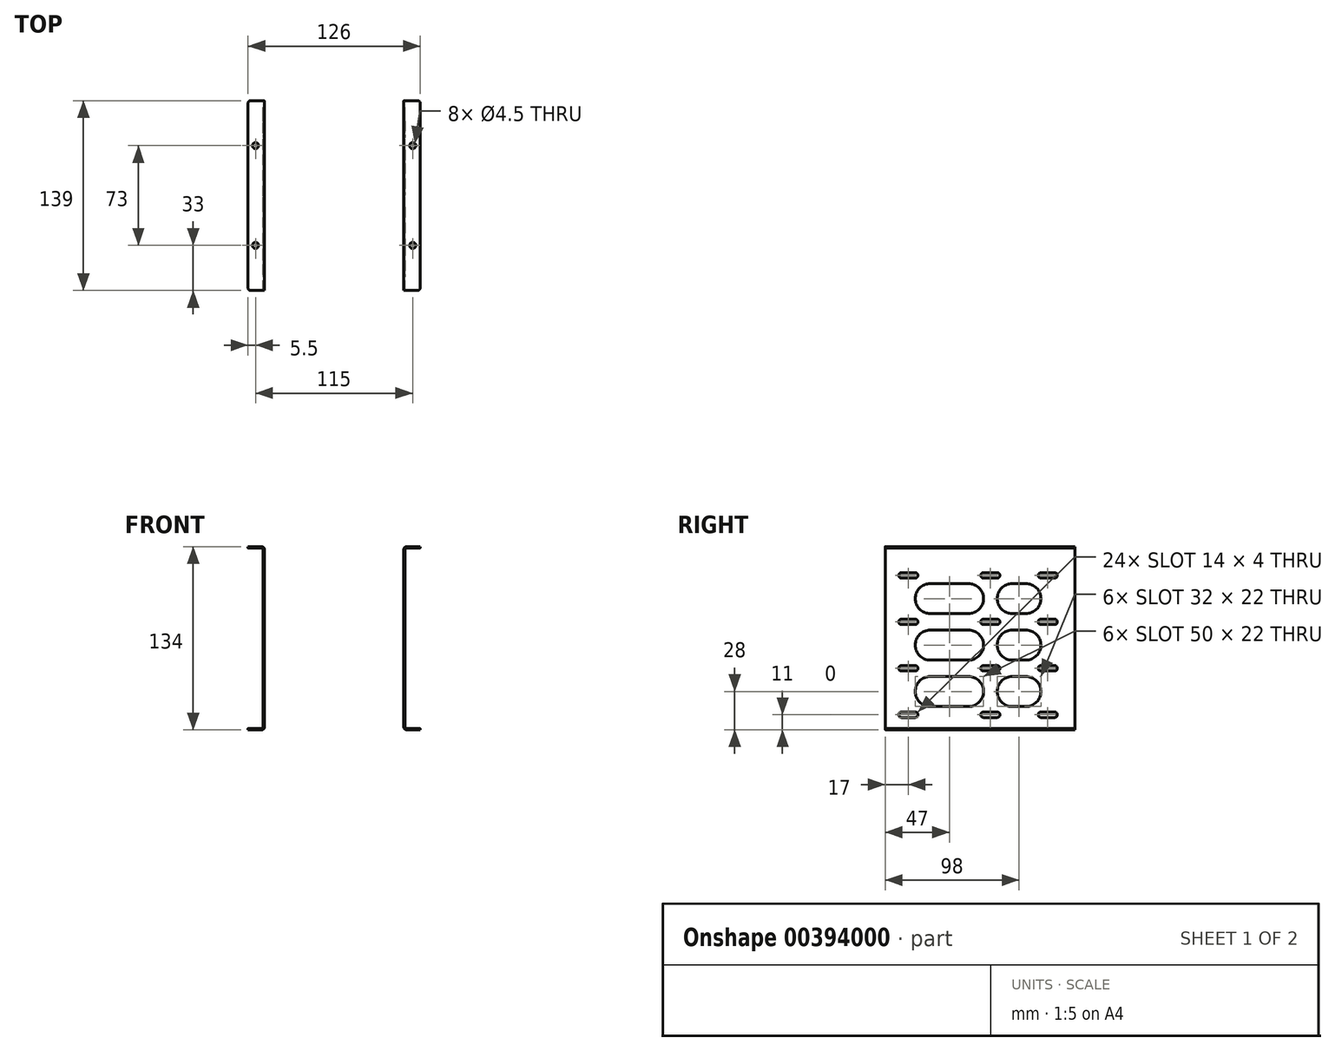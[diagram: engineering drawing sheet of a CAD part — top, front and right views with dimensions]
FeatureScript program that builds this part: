
annotation { "Feature Type Name" : "Feature", "Feature Type Description" : "" }
export const myFeature = defineFeature(function(context is Context, id is Id, definition is map)
    precondition{}
    {
        {
            var Q0;
            Q0=qCreatedBy(makeId("Front.planeOp"),FACE);
            var sketch = newSketch(context, id + "F0", { "sketchPlane" : qUnion([Q0])});
            skLineSegment(sketch, "E0", {"start": v(0, 0) * mm, "end": v(10, 0) * mm});
            skLineSegment(sketch, "E1", {"start": v(12, 2) * mm, "end": v(12, 132) * mm});
            skLineSegment(sketch, "E2", {"start": v(10, 134) * mm, "end": v(0, 134) * mm});
            skLineSegment(sketch, "E3.0", {"start": v(0, 1) * mm, "end": v(10, 1) * mm});
            skLineSegment(sketch, "E4.0", {"start": v(11, 2) * mm, "end": v(11, 132) * mm});
            skLineSegment(sketch, "E5.0", {"start": v(10, 133) * mm, "end": v(0, 133) * mm});
            skLineSegment(sketch, "E6", {"start": v(0, 133) * mm, "end": v(0, 134) * mm});
            skLineSegment(sketch, "E7", {"start": v(0, 0) * mm, "end": v(0, 1) * mm});
            skPoint(sketch, "E8.visualSharp", {"position": v(11, 1) * mm});
            skArc(sketch, "E8.filletArc", {"start": v(10, 1) * mm, "mid": v(10.7, 1.3) * mm, "end": v(11, 2) * mm});
            skPoint(sketch, "E9.visualSharp", {"position": v(12, 0) * mm});
            skArc(sketch, "E9.filletArc", {"start": v(10, 0) * mm, "mid": v(11.41, 0.59) * mm, "end": v(12, 2) * mm});
            skPoint(sketch, "E10.visualSharp", {"position": v(11, 133) * mm});
            skArc(sketch, "E10.filletArc", {"start": v(11, 132) * mm, "mid": v(10.7, 132.7) * mm, "end": v(10, 133) * mm});
            skPoint(sketch, "E11.visualSharp", {"position": v(12, 134) * mm});
            skArc(sketch, "E11.filletArc", {"start": v(12, 132) * mm, "mid": v(11.41, 133.41) * mm, "end": v(10, 134) * mm});
            skSolve(sketch);
        }
        {
            var Q0;
            Q0=qSketchRegion(id+"F0",true);
            extrude(context, id + "F1", {"entities" : qUnion([Q0]), "depth" : 139 * mm});
        }
        {
            var Q0;
            Q0=makeQuery(id+"F1.opExtrude","SWEPT_FACE",FACE,{"disambiguationData":[OSD([sQuery(id+"F0.wireOp",EDGE,"E2")])]});
            var sketch = newSketch(context, id + "F2", { "sketchPlane" : qUnion([Q0])});
            skCircle(sketch, "E12", {"center": v(5.5, -33) * mm, "radius": 2.25 * mm});
            skCircle(sketch, "E13.0.1.0", {"center": v(5.5, -106) * mm, "radius": 2.25 * mm});
            skLineSegment(sketch, "E13.direction1", {"start": v(5.5, -33) * mm, "end": v(30.5, -33) * mm, "construction": true});
            skLineSegment(sketch, "E13.direction2", {"start": v(5.5, -33) * mm, "end": v(5.5, -106) * mm, "construction": true});
            skSolve(sketch);
        }
        {
            var Q0;
            Q0=sQuery(id+"F2.wireOp",VERTEX,"E13.0.1.0.center");
            var Q1;
            Q1=sQuery(id+"F2.wireOp",VERTEX,"E12.center");
            var Q2;
            Q2=makeQuery(id+"F1.opExtrude","SWEPT_BODY",BODY,{"disambiguationData":[OSD([sQuery(id+"F0.wireOp",EDGE,"E0"),sQuery(id+"F0.wireOp",EDGE,"E1"),sQuery(id+"F0.wireOp",EDGE,"E2"),sQuery(id+"F0.wireOp",EDGE,"E3.0"),sQuery(id+"F0.wireOp",EDGE,"E4.0"),sQuery(id+"F0.wireOp",EDGE,"E5.0"),sQuery(id+"F0.wireOp",EDGE,"E6"),sQuery(id+"F0.wireOp",EDGE,"E7"),sQuery(id+"F0.wireOp",EDGE,"E8.filletArc"),sQuery(id+"F0.wireOp",EDGE,"E9.filletArc"),sQuery(id+"F0.wireOp",EDGE,"E10.filletArc"),sQuery(id+"F0.wireOp",EDGE,"E11.filletArc")])]});
            hole(context, id + "F3", {"style" : HoleStyle.SIMPLE, "endStyle" : HoleEndStyle.THROUGH, "holeDiameter" : 4.5 * mm, "isTappedThrough" : true, "tappedDepth" : 12 * mm, "tapClearance" : 3, "locations" : qUnion([Q0, Q1]), "scope" : qUnion([Q2])});
        }
        {
            var Q0;
            Q0=makeQuery(id+"F1.opExtrude","SWEPT_FACE",FACE,{"disambiguationData":[OSD([sQuery(id+"F0.wireOp",EDGE,"E4.0")])]});
            var sketch = newSketch(context, id + "F4", { "sketchPlane" : qUnion([Q0])});
            skLineSegment(sketch, "E14", {"start": v(15, 13) * mm, "end": v(25, 13) * mm});
            skLineSegment(sketch, "E15", {"start": v(15, 9) * mm, "end": v(25, 9) * mm});
            skArc(sketch, "E16", {"start": v(25, 13) * mm, "mid": v(27, 11) * mm, "end": v(25, 9) * mm});
            skArc(sketch, "E17", {"start": v(15, 13) * mm, "mid": v(13, 11) * mm, "end": v(15, 9) * mm});
            skPoint(sketch, "E18", {"position": v(20, 11) * mm});
            skPoint(sketch, "E19.0.1.0", {"position": v(20, 45) * mm});
            skArc(sketch, "E19.0.1.1", {"start": v(15, 47) * mm, "mid": v(13, 45) * mm, "end": v(15, 43) * mm});
            skLineSegment(sketch, "E19.0.1.2", {"start": v(15, 47) * mm, "end": v(25, 47) * mm});
            skLineSegment(sketch, "E19.0.1.3", {"start": v(15, 43) * mm, "end": v(25, 43) * mm});
            skArc(sketch, "E19.0.1.4", {"start": v(25, 47) * mm, "mid": v(27, 45) * mm, "end": v(25, 43) * mm});
            skPoint(sketch, "E19.0.2.0", {"position": v(20, 79) * mm});
            skArc(sketch, "E19.0.2.1", {"start": v(15, 81) * mm, "mid": v(13, 79) * mm, "end": v(15, 77) * mm});
            skLineSegment(sketch, "E19.0.2.2", {"start": v(15, 81) * mm, "end": v(25, 81) * mm});
            skLineSegment(sketch, "E19.0.2.3", {"start": v(15, 77) * mm, "end": v(25, 77) * mm});
            skArc(sketch, "E19.0.2.4", {"start": v(25, 81) * mm, "mid": v(27, 79) * mm, "end": v(25, 77) * mm});
            skPoint(sketch, "E19.0.3.0", {"position": v(20, 113) * mm});
            skArc(sketch, "E19.0.3.1", {"start": v(15, 115) * mm, "mid": v(13, 113) * mm, "end": v(15, 111) * mm});
            skLineSegment(sketch, "E19.0.3.2", {"start": v(15, 115) * mm, "end": v(25, 115) * mm});
            skLineSegment(sketch, "E19.0.3.3", {"start": v(15, 111) * mm, "end": v(25, 111) * mm});
            skArc(sketch, "E19.0.3.4", {"start": v(25, 115) * mm, "mid": v(27, 113) * mm, "end": v(25, 111) * mm});
            skPoint(sketch, "E19.1.0.0", {"position": v(62, 11) * mm});
            skArc(sketch, "E19.1.0.1", {"start": v(57, 13) * mm, "mid": v(55, 11) * mm, "end": v(57, 9) * mm});
            skLineSegment(sketch, "E19.1.0.2", {"start": v(57, 13) * mm, "end": v(67, 13) * mm});
            skLineSegment(sketch, "E19.1.0.3", {"start": v(57, 9) * mm, "end": v(67, 9) * mm});
            skArc(sketch, "E19.1.0.4", {"start": v(67, 13) * mm, "mid": v(69, 11) * mm, "end": v(67, 9) * mm});
            skPoint(sketch, "E19.1.1.0", {"position": v(62, 45) * mm});
            skArc(sketch, "E19.1.1.1", {"start": v(57, 47) * mm, "mid": v(55, 45) * mm, "end": v(57, 43) * mm});
            skLineSegment(sketch, "E19.1.1.2", {"start": v(57, 47) * mm, "end": v(67, 47) * mm});
            skLineSegment(sketch, "E19.1.1.3", {"start": v(57, 43) * mm, "end": v(67, 43) * mm});
            skArc(sketch, "E19.1.1.4", {"start": v(67, 47) * mm, "mid": v(69, 45) * mm, "end": v(67, 43) * mm});
            skPoint(sketch, "E19.1.2.0", {"position": v(62, 79) * mm});
            skArc(sketch, "E19.1.2.1", {"start": v(57, 81) * mm, "mid": v(55, 79) * mm, "end": v(57, 77) * mm});
            skLineSegment(sketch, "E19.1.2.2", {"start": v(57, 81) * mm, "end": v(67, 81) * mm});
            skLineSegment(sketch, "E19.1.2.3", {"start": v(57, 77) * mm, "end": v(67, 77) * mm});
            skArc(sketch, "E19.1.2.4", {"start": v(67, 81) * mm, "mid": v(69, 79) * mm, "end": v(67, 77) * mm});
            skPoint(sketch, "E19.1.3.0", {"position": v(62, 113) * mm});
            skArc(sketch, "E19.1.3.1", {"start": v(57, 115) * mm, "mid": v(55, 113) * mm, "end": v(57, 111) * mm});
            skLineSegment(sketch, "E19.1.3.2", {"start": v(57, 115) * mm, "end": v(67, 115) * mm});
            skLineSegment(sketch, "E19.1.3.3", {"start": v(57, 111) * mm, "end": v(67, 111) * mm});
            skArc(sketch, "E19.1.3.4", {"start": v(67, 115) * mm, "mid": v(69, 113) * mm, "end": v(67, 111) * mm});
            skLineSegment(sketch, "E19.direction1", {"start": v(20, 11) * mm, "end": v(62, 11) * mm, "construction": true});
            skLineSegment(sketch, "E19.direction2", {"start": v(20, 11) * mm, "end": v(20, 45) * mm, "construction": true});
            skPoint(sketch, "E20.1.0.0", {"position": v(122, 11) * mm});
            skLineSegment(sketch, "E20.1.0.1", {"start": v(117, 13) * mm, "end": v(127, 13) * mm});
            skArc(sketch, "E20.1.0.2", {"start": v(117, 13) * mm, "mid": v(115, 11) * mm, "end": v(117, 9) * mm});
            skLineSegment(sketch, "E20.1.0.3", {"start": v(117, 9) * mm, "end": v(127, 9) * mm});
            skArc(sketch, "E20.1.0.4", {"start": v(127, 13) * mm, "mid": v(129, 11) * mm, "end": v(127, 9) * mm});
            skPoint(sketch, "E20.1.1.0", {"position": v(122, 45) * mm});
            skLineSegment(sketch, "E20.1.1.1", {"start": v(117, 47) * mm, "end": v(127, 47) * mm});
            skArc(sketch, "E20.1.1.2", {"start": v(117, 47) * mm, "mid": v(115, 45) * mm, "end": v(117, 43) * mm});
            skLineSegment(sketch, "E20.1.1.3", {"start": v(117, 43) * mm, "end": v(127, 43) * mm});
            skArc(sketch, "E20.1.1.4", {"start": v(127, 47) * mm, "mid": v(129, 45) * mm, "end": v(127, 43) * mm});
            skPoint(sketch, "E20.1.2.0", {"position": v(122, 79) * mm});
            skLineSegment(sketch, "E20.1.2.1", {"start": v(117, 81) * mm, "end": v(127, 81) * mm});
            skArc(sketch, "E20.1.2.2", {"start": v(117, 81) * mm, "mid": v(115, 79) * mm, "end": v(117, 77) * mm});
            skLineSegment(sketch, "E20.1.2.3", {"start": v(117, 77) * mm, "end": v(127, 77) * mm});
            skArc(sketch, "E20.1.2.4", {"start": v(127, 81) * mm, "mid": v(129, 79) * mm, "end": v(127, 77) * mm});
            skPoint(sketch, "E20.1.3.0", {"position": v(122, 113) * mm});
            skLineSegment(sketch, "E20.1.3.1", {"start": v(117, 115) * mm, "end": v(127, 115) * mm});
            skArc(sketch, "E20.1.3.2", {"start": v(117, 115) * mm, "mid": v(115, 113) * mm, "end": v(117, 111) * mm});
            skLineSegment(sketch, "E20.1.3.3", {"start": v(117, 111) * mm, "end": v(127, 111) * mm});
            skArc(sketch, "E20.1.3.4", {"start": v(127, 115) * mm, "mid": v(129, 113) * mm, "end": v(127, 111) * mm});
            skLineSegment(sketch, "E20.direction1", {"start": v(62, 11) * mm, "end": v(122, 11) * mm, "construction": true});
            skLineSegment(sketch, "E20.direction2", {"start": v(62, 11) * mm, "end": v(62, 45) * mm, "construction": true});
            skSolve(sketch);
        }
        {
            var Q0;
            Q0=qSketchRegion(id+"F4",true);
            extrude(context, id + "F5", {"entities" : qUnion([Q0]), "operationType" : NewBodyOperationType.REMOVE, "oppositeDirection" : true, "depth" : 25 * mm});
        }
        {
            var Q0;
            Q0=makeQuery(id+"F1.opExtrude","CAP_EDGE",EDGE,{"disambiguationData":[OSD([sQuery(id+"F0.wireOp",EDGE,"E6")])],"isStart":false});
            fillet(context, id + "F6", {"entities" : qUnion([Q0]), "radius" : 2 * mm, "tangentPropagation" : true, "allowEdgeOverflow" : false});
        }
        {
            var Q0;
            Q0=makeQuery(id+"F1.opExtrude","CAP_EDGE",EDGE,{"disambiguationData":[OSD([sQuery(id+"F0.wireOp",EDGE,"E7")])],"isStart":false});
            fillet(context, id + "F7", {"entities" : qUnion([Q0]), "radius" : 2 * mm, "allowEdgeOverflow" : false});
        }
        {
            var Q0;
            Q0=makeQuery(id+"F1.opExtrude","CAP_EDGE",EDGE,{"disambiguationData":[OSD([sQuery(id+"F0.wireOp",EDGE,"E7")])],"isStart":true});
            fillet(context, id + "F8", {"entities" : qUnion([Q0]), "radius" : 2 * mm, "tangentPropagation" : true, "allowEdgeOverflow" : false});
        }
        {
            var Q0;
            Q0=makeQuery(id+"F1.opExtrude","CAP_EDGE",EDGE,{"disambiguationData":[OSD([sQuery(id+"F0.wireOp",EDGE,"E6")])],"isStart":true});
            fillet(context, id + "F9", {"entities" : qUnion([Q0]), "radius" : 2 * mm, "tangentPropagation" : true, "allowEdgeOverflow" : false});
        }
        {
            var Q0;
            Q0=makeQuery(id+"F1.opExtrude","SWEPT_FACE",FACE,{"disambiguationData":[OSD([sQuery(id+"F0.wireOp",EDGE,"E4.0")])]});
            var sketch = newSketch(context, id + "F10", { "sketchPlane" : qUnion([Q0])});
            skLineSegment(sketch, "E21", {"start": v(36, 39) * mm, "end": v(46, 39) * mm});
            skLineSegment(sketch, "E22", {"start": v(36, 17) * mm, "end": v(46, 17) * mm});
            skArc(sketch, "E23", {"start": v(36, 39) * mm, "mid": v(25, 28) * mm, "end": v(36, 17) * mm});
            skArc(sketch, "E24", {"start": v(46, 39) * mm, "mid": v(57, 28) * mm, "end": v(46, 17) * mm});
            skPoint(sketch, "E25", {"position": v(41, 28) * mm});
            skPoint(sketch, "E26.0.1.0", {"position": v(41, 62) * mm});
            skLineSegment(sketch, "E26.0.1.1", {"start": v(36, 73) * mm, "end": v(46, 73) * mm});
            skArc(sketch, "E26.0.1.2", {"start": v(36, 73) * mm, "mid": v(25, 62) * mm, "end": v(36, 51) * mm});
            skLineSegment(sketch, "E26.0.1.3", {"start": v(36, 51) * mm, "end": v(46, 51) * mm});
            skArc(sketch, "E26.0.1.4", {"start": v(46, 73) * mm, "mid": v(57, 62) * mm, "end": v(46, 51) * mm});
            skPoint(sketch, "E26.0.2.0", {"position": v(41, 96) * mm});
            skLineSegment(sketch, "E26.0.2.1", {"start": v(36, 107) * mm, "end": v(46, 107) * mm});
            skArc(sketch, "E26.0.2.2", {"start": v(36, 107) * mm, "mid": v(25, 96) * mm, "end": v(36, 85) * mm});
            skLineSegment(sketch, "E26.0.2.3", {"start": v(36, 85) * mm, "end": v(46, 85) * mm});
            skArc(sketch, "E26.0.2.4", {"start": v(46, 107) * mm, "mid": v(57, 96) * mm, "end": v(46, 85) * mm});
            skLineSegment(sketch, "E26.direction1", {"start": v(36, 17) * mm, "end": v(61, 17) * mm, "construction": true});
            skLineSegment(sketch, "E26.direction2", {"start": v(36, 17) * mm, "end": v(36, 51) * mm, "construction": true});
            skLineSegment(sketch, "E27", {"start": v(78, 39) * mm, "end": v(106, 39) * mm});
            skLineSegment(sketch, "E28", {"start": v(78, 17) * mm, "end": v(106, 17) * mm});
            skArc(sketch, "E29", {"start": v(78, 39) * mm, "mid": v(67, 28) * mm, "end": v(78, 17) * mm});
            skArc(sketch, "E30", {"start": v(106, 39) * mm, "mid": v(117, 28) * mm, "end": v(106, 17) * mm});
            skPoint(sketch, "E31", {"position": v(92, 28) * mm});
            skPoint(sketch, "E32.0.1.0", {"position": v(92, 62) * mm});
            skLineSegment(sketch, "E32.0.1.1", {"start": v(78, 51) * mm, "end": v(106, 51) * mm});
            skLineSegment(sketch, "E32.0.1.2", {"start": v(78, 73) * mm, "end": v(106, 73) * mm});
            skArc(sketch, "E32.0.1.3", {"start": v(78, 73) * mm, "mid": v(67, 62) * mm, "end": v(78, 51) * mm});
            skArc(sketch, "E32.0.1.4", {"start": v(106, 73) * mm, "mid": v(117, 62) * mm, "end": v(106, 51) * mm});
            skPoint(sketch, "E32.0.2.0", {"position": v(92, 96) * mm});
            skLineSegment(sketch, "E32.0.2.1", {"start": v(78, 85) * mm, "end": v(106, 85) * mm});
            skLineSegment(sketch, "E32.0.2.2", {"start": v(78, 107) * mm, "end": v(106, 107) * mm});
            skArc(sketch, "E32.0.2.3", {"start": v(78, 107) * mm, "mid": v(67, 96) * mm, "end": v(78, 85) * mm});
            skArc(sketch, "E32.0.2.4", {"start": v(106, 107) * mm, "mid": v(117, 96) * mm, "end": v(106, 85) * mm});
            skLineSegment(sketch, "E32.direction1", {"start": v(78, 17) * mm, "end": v(103, 17) * mm, "construction": true});
            skLineSegment(sketch, "E32.direction2", {"start": v(78, 17) * mm, "end": v(78, 51) * mm, "construction": true});
            skSolve(sketch);
        }
        {
            var Q0;
            Q0=qSketchRegion(id+"F10",true);
            extrude(context, id + "F11", {"entities" : qUnion([Q0]), "operationType" : NewBodyOperationType.REMOVE, "oppositeDirection" : true, "depth" : 25 * mm});
        }
        {
            var Q0;
            Q0=qCreatedBy(makeId("Right.planeOp"),FACE);
            cPlane(context, id + "F12", {"entities" : qUnion([Q0]), "cplaneType" : CPlaneType.OFFSET, "offset" : 63 * mm, "width" : 150 * mm, "height" : 150 * mm});
        }
        {
            var Q0;
            Q0=makeQuery(id+"F1.opExtrude","SWEPT_BODY",BODY,{"disambiguationData":[OSD([sQuery(id+"F0.wireOp",EDGE,"E0"),sQuery(id+"F0.wireOp",EDGE,"E1"),sQuery(id+"F0.wireOp",EDGE,"E2"),sQuery(id+"F0.wireOp",EDGE,"E3.0"),sQuery(id+"F0.wireOp",EDGE,"E4.0"),sQuery(id+"F0.wireOp",EDGE,"E5.0"),sQuery(id+"F0.wireOp",EDGE,"E6"),sQuery(id+"F0.wireOp",EDGE,"E7"),sQuery(id+"F0.wireOp",EDGE,"E8.filletArc"),sQuery(id+"F0.wireOp",EDGE,"E9.filletArc"),sQuery(id+"F0.wireOp",EDGE,"E10.filletArc"),sQuery(id+"F0.wireOp",EDGE,"E11.filletArc")])]});
            var Q1;
            Q1=qCreatedBy(id+"F12.planeOp",FACE);
            mirror(context, id + "F13", {"entities" : qUnion([Q0]), "mirrorPlane" : qUnion([Q1])});
        }
    });
